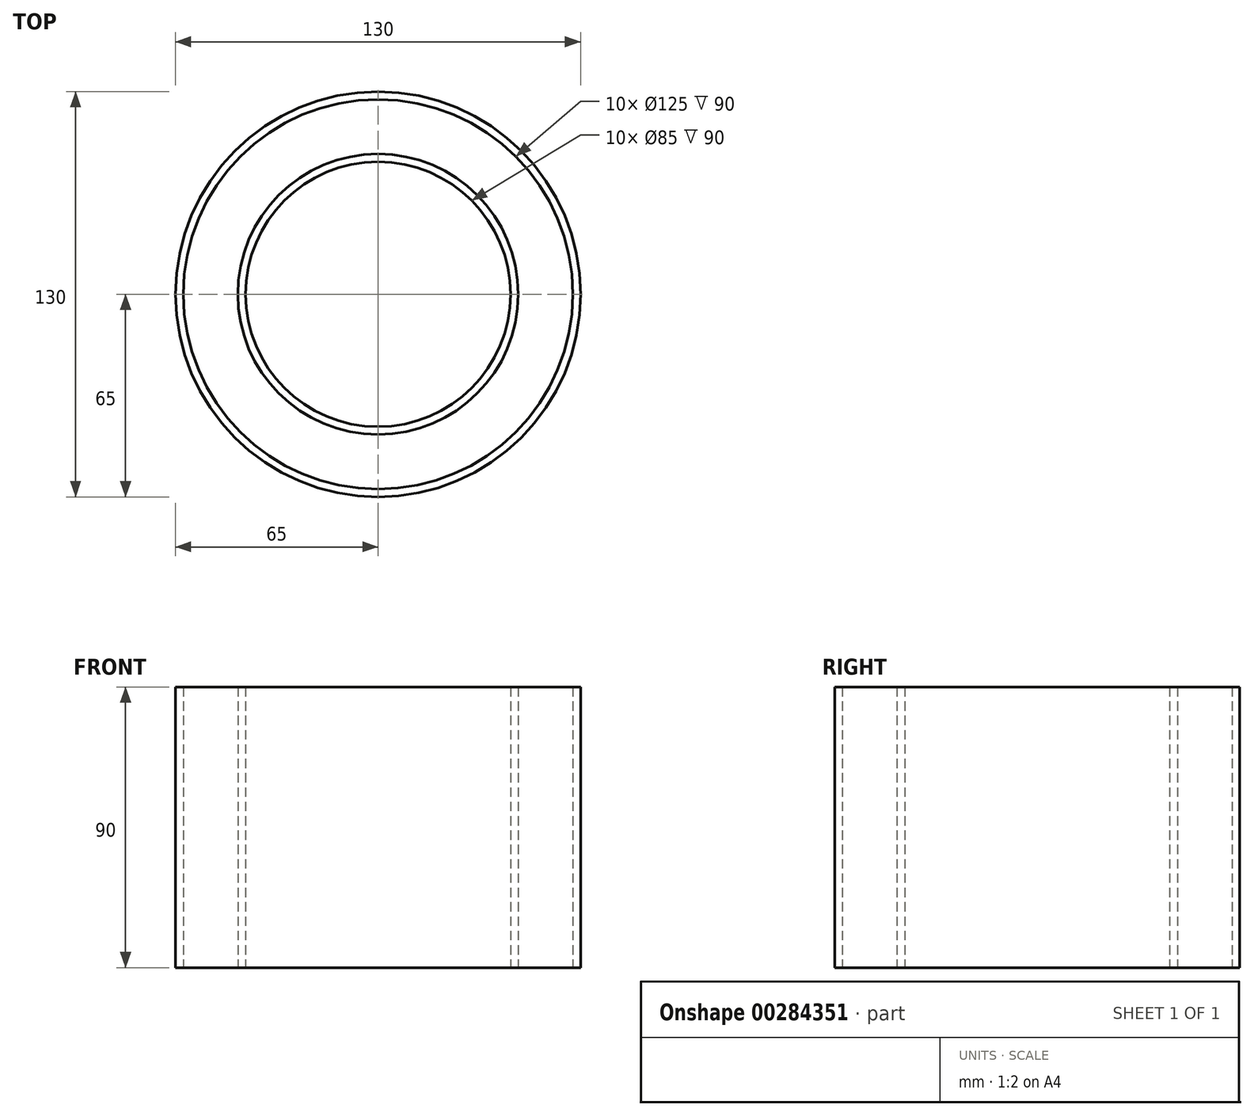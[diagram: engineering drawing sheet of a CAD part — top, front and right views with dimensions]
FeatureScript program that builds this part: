
annotation { "Feature Type Name" : "Feature", "Feature Type Description" : "" }
export const myFeature = defineFeature(function(context is Context, id is Id, definition is map)
    precondition{}
    {
        {
            var Q0;
            Q0=qCreatedBy(makeId("Top.planeOp"),FACE);
            var sketch = newSketch(context, id + "F0", { "sketchPlane" : qUnion([Q0])});
            skCircle(sketch, "E0", {"center": v(0, 0) * mm, "radius": 45 * mm});
            skCircle(sketch, "E1", {"center": v(0, 0) * mm, "radius": 42.5 * mm});
            skCircle(sketch, "E2", {"center": v(0, 0) * mm, "radius": 65 * mm});
            skCircle(sketch, "E3", {"center": v(0, 0) * mm, "radius": 62.5 * mm});
            skSolve(sketch);
        }
        {
            var Q0;
            Q0=makeQuery(id+"F0.imprint","IMPRINT",FACE,{"disambiguationData":[TD([[makeQuery(id+"F0.imprint","IMPRINT",EDGE,{"derivedFrom":sQuery(id+"F0.wireOp",EDGE,"E2")}),1.0]])]});
            var Q1;
            Q1=makeQuery(id+"F0.imprint","IMPRINT",FACE,{"disambiguationData":[TD([[makeQuery(id+"F0.imprint","IMPRINT",EDGE,{"derivedFrom":sQuery(id+"F0.wireOp",EDGE,"E0")}),1.0]])]});
            extrude(context, id + "F1", {"entities" : qUnion([Q0, Q1]), "depth" : 90 * mm});
        }
        {
            var Q0;
            Q0=qCreatedBy(makeId("Top.planeOp"),FACE);
            var sketch = newSketch(context, id + "F2", { "sketchPlane" : qUnion([Q0])});
            skLineSegment(sketch, "E4.bottom", {"start": v(-65, 0) * mm, "end": v(65, 0) * mm});
            skLineSegment(sketch, "E4.top", {"start": v(-65, -65) * mm, "end": v(65, -65) * mm});
            skLineSegment(sketch, "E4.left", {"start": v(-65, 0) * mm, "end": v(-65, -65) * mm});
            skLineSegment(sketch, "E4.right", {"start": v(65, 0) * mm, "end": v(65, -65) * mm});
            skSolve(sketch);
        }
        {
            var Q0;
            Q0=makeQuery(id+"F2.imprint","IMPRINT",FACE,{"disambiguationData":[TD([[makeQuery(id+"F2.imprint","IMPRINT",EDGE,{"derivedFrom":sQuery(id+"F2.wireOp",EDGE,"E4.bottom")}),-1.0]])]});
            extrude(context, id + "F3", {"entities" : qUnion([Q0]), "operationType" : NewBodyOperationType.REMOVE, "endBound" : BoundingType.THROUGH_ALL, "oppositeDirection" : true, "depth" : 90 * mm});
        }
    });
